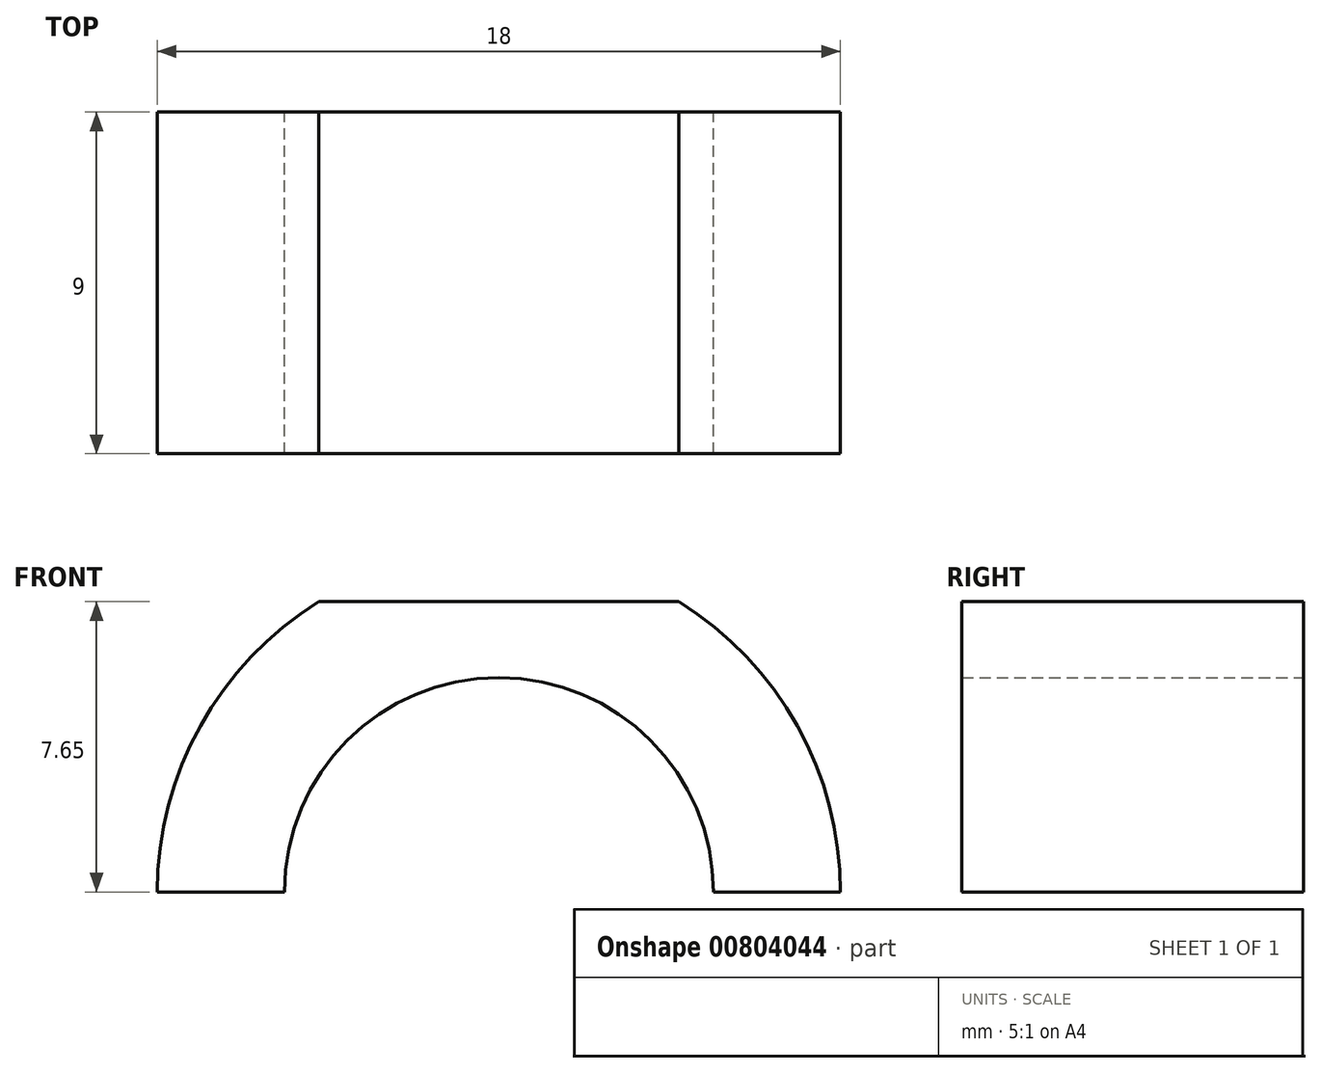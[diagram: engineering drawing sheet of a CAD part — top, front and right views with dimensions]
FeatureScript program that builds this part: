
annotation { "Feature Type Name" : "Feature", "Feature Type Description" : "" }
export const myFeature = defineFeature(function(context is Context, id is Id, definition is map)
    precondition{}
    {
        {
            var Q0;
            Q0=qCreatedBy(makeId("Front.planeOp"),FACE);
            var sketch = newSketch(context, id + "F0", { "sketchPlane" : qUnion([Q0])});
            skCircle(sketch, "E0", {"center": v(0, 0) * mm, "radius": 9 * mm});
            skCircle(sketch, "E1", {"center": v(0, 0) * mm, "radius": 5.65 * mm});
            skSolve(sketch);
        }
        {
            var Q0;
            Q0 = qSketchRegion(id + "F0", true);
            extrude(context, id + "F1", {"entities" : qUnion([Q0]), "depth" : 9 * mm, "offsetDistance" : 25 * mm});
        }
        {
            var Q0;
            Q0=makeQuery(id+"F1.opExtrude","CAP_FACE",FACE,{"disambiguationData":[OSD([sQuery(id+"F0.wireOp",EDGE,"E0"),sQuery(id+"F0.wireOp",EDGE,"E1")])],"isStart":false});
            var sketch = newSketch(context, id + "F2", { "sketchPlane" : qUnion([Q0])});
            skLineSegment(sketch, "E2", {"start": v(-9, 0) * mm, "end": v(9.6, 0) * mm});
            skLineSegment(sketch, "E3", {"start": v(9.6, 0) * mm, "end": v(9.6, -10.8) * mm});
            skLineSegment(sketch, "E4", {"start": v(9.6, -10.8) * mm, "end": v(-9.97, -10.8) * mm});
            skLineSegment(sketch, "E5", {"start": v(-9.97, -10.8) * mm, "end": v(-9.97, 0) * mm});
            skLineSegment(sketch, "E6", {"start": v(-9.97, 0) * mm, "end": v(-9, 0) * mm});
            skSolve(sketch);
        }
        {
            var Q0;
            Q0 = qSketchRegion(id + "F2", true);
            extrude(context, id + "F3", {"entities" : qUnion([Q0]), "operationType" : NewBodyOperationType.REMOVE, "oppositeDirection" : true, "depth" : 25 * mm, "offsetDistance" : 25 * mm});
        }
        {
            var Q0;
            Q0=makeQuery(id+"F1.opExtrude","CAP_FACE",FACE,{"disambiguationData":[OSD([sQuery(id+"F0.wireOp",EDGE,"E0"),sQuery(id+"F0.wireOp",EDGE,"E1")])],"isStart":false});
            var sketch = newSketch(context, id + "F4", { "sketchPlane" : qUnion([Q0])});
            skPoint(sketch, "E7", {"position": v(0, 7.65) * mm});
            skLineSegment(sketch, "E8", {"start": v(0, 7.65) * mm, "end": v(5.87, 7.65) * mm});
            skLineSegment(sketch, "E9", {"start": v(5.87, 7.65) * mm, "end": v(5.87, 11.9) * mm});
            skLineSegment(sketch, "E10", {"start": v(5.87, 11.9) * mm, "end": v(-7.13, 11.9) * mm});
            skLineSegment(sketch, "E11", {"start": v(-7.13, 11.9) * mm, "end": v(-7.13, 7.65) * mm});
            skLineSegment(sketch, "E12", {"start": v(-7.13, 7.65) * mm, "end": v(0, 7.65) * mm});
            skSolve(sketch);
        }
        {
            var Q0;
            Q0 = qSketchRegion(id + "F4", true);
            extrude(context, id + "F5", {"entities" : qUnion([Q0]), "operationType" : NewBodyOperationType.REMOVE, "oppositeDirection" : true, "depth" : 25 * mm, "offsetDistance" : 25 * mm});
        }
    });
